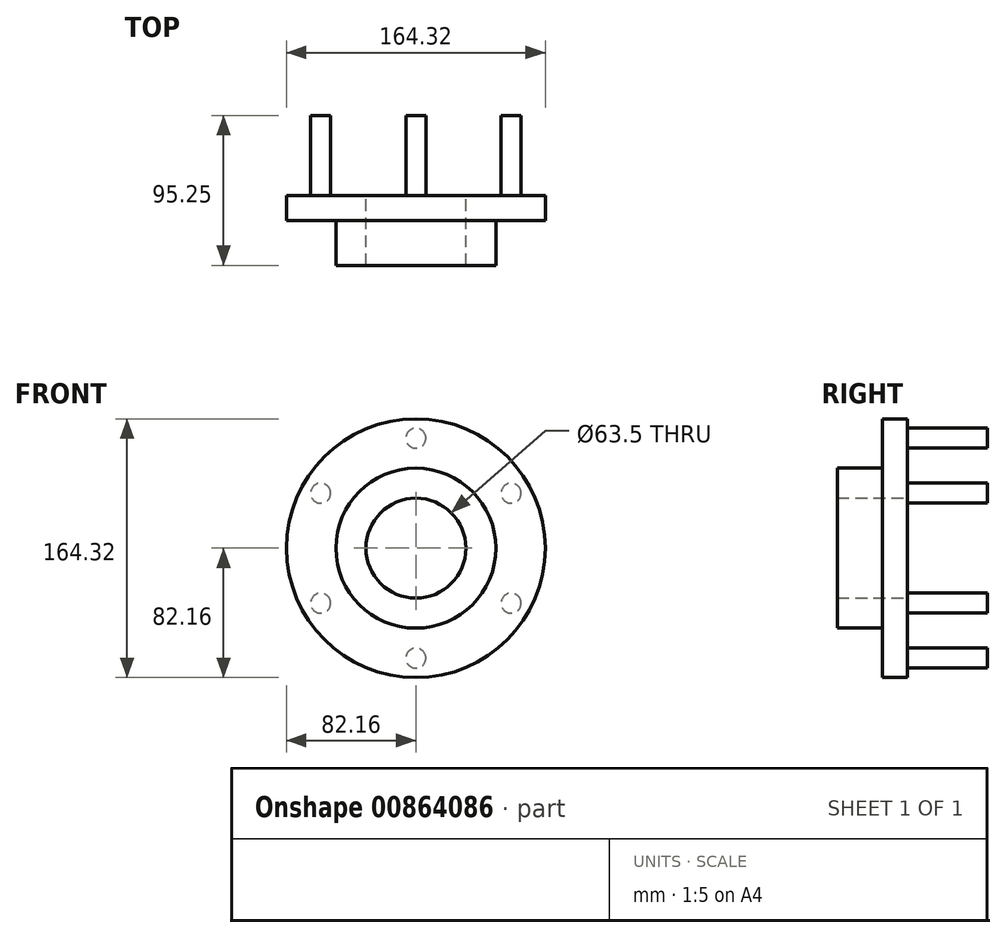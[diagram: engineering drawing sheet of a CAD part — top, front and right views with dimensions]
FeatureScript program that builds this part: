
annotation { "Feature Type Name" : "Feature", "Feature Type Description" : "" }
export const myFeature = defineFeature(function(context is Context, id is Id, definition is map)
    precondition{}
    {
        {
            var Q0;
            Q0=qCreatedBy(makeId("Front.planeOp"),FACE);
            var sketch = newSketch(context, id + "F0", { "sketchPlane" : qUnion([Q0])});
            skCircle(sketch, "E0", {"center": v(0, 0) * mm, "radius": 69.85 * mm, "construction": true});
            skCircle(sketch, "E1", {"center": v(0, 69.85) * mm, "radius": 6.35 * mm});
            skCircle(sketch, "E2.1.0", {"center": v(-60.5, 34.93) * mm, "radius": 6.35 * mm});
            skCircle(sketch, "E2.2.0", {"center": v(-60.5, -34.92) * mm, "radius": 6.35 * mm});
            skCircle(sketch, "E2.3.0", {"center": v(0, -69.85) * mm, "radius": 6.35 * mm});
            skCircle(sketch, "E2.4.0", {"center": v(60.5, -34.93) * mm, "radius": 6.35 * mm});
            skCircle(sketch, "E2.5.0", {"center": v(60.5, 34.93) * mm, "radius": 6.35 * mm});
            skCircle(sketch, "E3", {"center": v(0, 0) * mm, "radius": 82.16 * mm});
            skCircle(sketch, "E4", {"center": v(0, 0) * mm, "radius": 50.8 * mm});
            skCircle(sketch, "E5", {"center": v(0, 0) * mm, "radius": 31.75 * mm});
            skCircle(sketch, "E6", {"center": v(0, 0) * mm, "radius": 19.05 * mm});
            skSolve(sketch);
        }
        {
            var Q0;
            Q0=makeQuery(id+"F0.imprint","IMPRINT",FACE,{"disambiguationData":[TD([[makeQuery(id+"F0.imprint","IMPRINT",EDGE,{"derivedFrom":sQuery(id+"F0.wireOp",EDGE,"E1")}),-1.0]])]});
            extrude(context, id + "F1", {"entities" : qUnion([Q0]), "depth" : 15.88 * mm, "offsetDistance" : 25.4 * mm});
        }
        {
            var Q0;
            Q0=makeQuery(id+"F0.imprint","IMPRINT",FACE,{"disambiguationData":[TD([[makeQuery(id+"F0.imprint","IMPRINT",EDGE,{"derivedFrom":sQuery(id+"F0.wireOp",EDGE,"E4")}),1.0]])]});
            extrude(context, id + "F2", {"entities" : qUnion([Q0]), "operationType" : NewBodyOperationType.ADD, "depth" : 44.45 * mm, "offsetDistance" : 25.4 * mm});
        }
        {
            var Q0;
            Q0=makeQuery(id+"F0.imprint","IMPRINT",FACE,{"disambiguationData":[TD([[makeQuery(id+"F0.imprint","IMPRINT",EDGE,{"derivedFrom":sQuery(id+"F0.wireOp",EDGE,"E2.1.0")}),1.0]])]});
            var Q1;
            Q1=makeQuery(id+"F0.imprint","IMPRINT",FACE,{"disambiguationData":[TD([[makeQuery(id+"F0.imprint","IMPRINT",EDGE,{"derivedFrom":sQuery(id+"F0.wireOp",EDGE,"E1")}),1.0]])]});
            var Q2;
            Q2=makeQuery(id+"F0.imprint","IMPRINT",FACE,{"disambiguationData":[TD([[makeQuery(id+"F0.imprint","IMPRINT",EDGE,{"derivedFrom":sQuery(id+"F0.wireOp",EDGE,"E2.5.0")}),1.0]])]});
            var Q3;
            Q3=makeQuery(id+"F0.imprint","IMPRINT",FACE,{"disambiguationData":[TD([[makeQuery(id+"F0.imprint","IMPRINT",EDGE,{"derivedFrom":sQuery(id+"F0.wireOp",EDGE,"E2.4.0")}),1.0]])]});
            var Q4;
            Q4=makeQuery(id+"F0.imprint","IMPRINT",FACE,{"disambiguationData":[TD([[makeQuery(id+"F0.imprint","IMPRINT",EDGE,{"derivedFrom":sQuery(id+"F0.wireOp",EDGE,"E2.3.0")}),1.0]])]});
            var Q5;
            Q5=makeQuery(id+"F0.imprint","IMPRINT",FACE,{"disambiguationData":[TD([[makeQuery(id+"F0.imprint","IMPRINT",EDGE,{"derivedFrom":sQuery(id+"F0.wireOp",EDGE,"E2.2.0")}),1.0]])]});
            extrude(context, id + "F3", {"entities" : qUnion([Q0, Q1, Q2, Q3, Q4, Q5]), "operationType" : NewBodyOperationType.ADD, "depth" : 15.88 * mm, "offsetDistance" : 25.4 * mm, "hasSecondDirection" : true, "secondDirectionOppositeDirection" : true, "secondDirectionDepth" : 50.8 * mm});
        }
    });
